# Revit family: 18-70-003 DN150
name_source: partatom
category: Pipe Accessories
units: mm (PartAtom-declared; Revit-internal decimal feet)

## family parameters
Always vertical = Yes
Cut with Voids When Loaded = No
Part Type = Valve - Breaks Into
Round Connector Dimension = Use Diameter
Shared = No
Work Plane-Based = No

## types (1)
- DN150_PN10/16
    1 = 1 mm  [stored 0.00328084 ft]
    20 = 20 mm  [stored 0.0656168 ft]
    27 = 27 mm  [stored 0.0885827 ft]
    5 = 5 mm  [stored 0.0164042 ft]
    50 = 50 mm  [stored 0.164042 ft]
    Body_H = 172 mm  [stored 0.564304 ft]
    Bore_R = 75 mm  [stored 0.246063 ft]
    DN = 150 mm  [stored 0.492126 ft]
    DN150_PN10/16 = 18-150-70-0140000099
    Default Elevation = 0 mm  [stored 0 ft]
    Description_ = AVK COMBI-CROSS, FLANGED, 4 OUTLETS, PN10/16
    Dh = 240 mm  [stored 0.787402 ft]
    F = 10 mm  [stored 0.0328084 ft]
    F1 = 13 mm
    F2 = 45 mm  [stored 0.147638 ft]
    F3 = 35 mm  [stored 0.114829 ft]
    FL_R = 143 mm
    FL_T = 18 mm  [stored 0.0590551 ft]
    H = 400 mm  [stored 1.31234 ft]
    H1 = 275 mm  [stored 0.902231 ft]
    H3 = 543 mm  [stored 1.7815 ft]
    H3-H = 143 mm
    L = 620 mm  [stored 2.03412 ft]
    L-L1 = 124 mm  [stored 0.406824 ft]
    L1 = 372 mm  [stored 1.22047 ft]
    L2 = 180 mm  [stored 0.590551 ft]
    L5 = 243 mm
    L6 = 216 mm  [stored 0.708661 ft]
    L_half = 155 mm  [stored 0.50853 ft]
    OD = 142 mm  [stored 0.465879 ft]
    OD1 = 78 mm  [stored 0.255906 ft]
    OD2 = 86 mm  [stored 0.282152 ft]
    P1 = 263 mm  [stored 0.862861 ft]
    Raised_R = 106 mm  [stored 0.347769 ft]
    Raised_dis = 3 mm  [stored 0.00984252 ft]
    Search_table = 18-70-003 DN150
    URL_product_pages = https://www.avkvalves.com
    W = 143 mm
    arc = 200 mm  [stored 0.656168 ft]
    arc1 = 63 mm  [stored 0.206693 ft]
    arc2 = 126 mm  [stored 0.413386 ft]
    body_dim1 = 135 mm
    main_dim1 = 94 mm  [stored 0.308399 ft]

note: [stored X ft] marks values corroborated as IEEE doubles in the binary element streams (Revit-internal decimal feet)

## geometry (parser evidence)
native form markers: Sweep x5
no freeform markers — native parametric forms only
